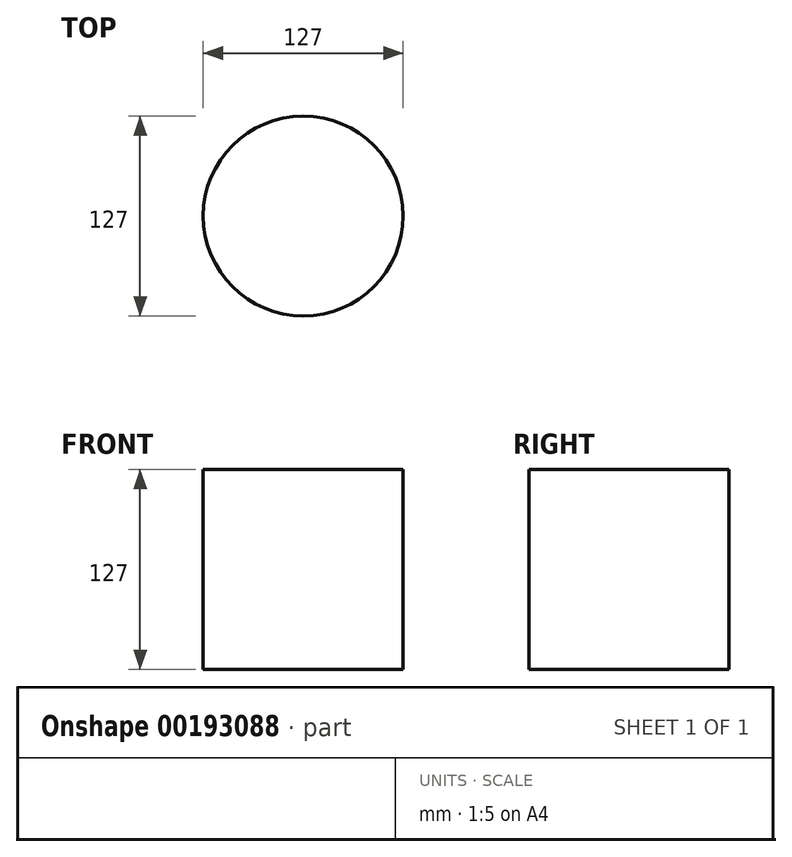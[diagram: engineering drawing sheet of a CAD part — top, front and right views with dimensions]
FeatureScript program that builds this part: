
annotation { "Feature Type Name" : "Feature", "Feature Type Description" : "" }
export const myFeature = defineFeature(function(context is Context, id is Id, definition is map)
    precondition{}
    {
        {
            var Q0;
            Q0=qCreatedBy(makeId("Top.planeOp"),FACE);
            var sketch = newSketch(context, id + "F0", { "sketchPlane" : qUnion([Q0])});
            skCircle(sketch, "E0", {"center": v(0, 0) * mm, "radius": 63.5 * mm});
            skSolve(sketch);
        }
        {
            var Q0;
            Q0=makeQuery(id+"F0.imprint","IMPRINT",FACE,{"disambiguationData":[TD([[makeQuery(id+"F0.imprint","IMPRINT",EDGE,{"derivedFrom":sQuery(id+"F0.wireOp",EDGE,"E0")}),1.0]])]});
            extrude(context, id + "F1", {"entities" : qUnion([Q0]), "depth" : 127 * mm});
        }
    });
